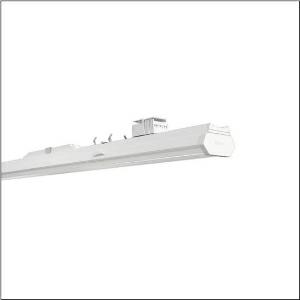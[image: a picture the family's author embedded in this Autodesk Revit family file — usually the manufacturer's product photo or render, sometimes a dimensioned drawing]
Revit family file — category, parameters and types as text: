
# Revit family: licross_21_protected_mo_52tp12dn4a5gd
name_source: partatom
category: Lighting Fixtures
units: mm (PartAtom-declared; Revit-internal decimal feet)

## family parameters
Cut with Voids When Loaded = No
Host = Face
Light Source = No
Part Type = Normal
Room Calculation Point = No
Round Connector Dimension = Use Diameter
Shared = No

## types (1)
- --- (1 x LED, 1610 lm, 10.2 W, 4000K)
    Apparent Load = 10 VA
    CIE Flux Codes = 73 92 98 99 100
    Color Rendering = 80
    Color Temperature = 4000K
    Default Elevation = 1800 mm
    Description = Licross 21 Protected MO, luminaire insert, of sheet steel, galvanised, coil coated, white, length: 1.500mm, width: 90mm, height: 103mm, LED rated luminous flux: 10.700lm, light colour: 840, SDCM (Standard Deviation of Colour Matching)MacAdam ≤ 3 SDCM (initial), control gear: DALI 2 (for two DALI lines), with plug, 6-pole, with phase selection, mains connection: 220..240V, AC/DC, 0/50..60Hz, rated input power: 62W, without changeover relay, for emergency light function, for central battery installations according to EN 60598-2-22, internal wiring halogen-free, primary light control with lens, of plastic, primary optical cover: cover, of PMMA, light emission: direct distribution, primary light characteristic: symmetric, protection rating (complete): IP64, insulation class (complete): insulation class I (protective earthing), certification: CE, ENEC, VDE, UKCA, protection symbol: D if used in an environment with conductive dust loads with corresponding accessories, impact resistance: IK06, permissible ambient temperature for indoor applications: -25..+35°C, standard: EN 60598-2-22, corresponds to IFS (International Featured Standards) requirements for safety and quality in the food industry, reducing of maximum allowable ambient temperature of 5°C with ceiling mounting, LABS conformity tested according to VDMA 24364:2018-05, The light source and the operating device comply with the requirements of the Ecodesign Regulation (EU) 2019/2020 and are replaceable in accordance with this regulation, packaging unit: 1 piece
    Height = 92 mm
    Lamp = 1 x LED
    Lamp Light Flux = 1610 lm
    Lamp Power = 10.2 W
    Lamp count = 1
    Length = 1500 mm
    Luminous efficacy = 158 lm/W
    Manufacturer = Siteco
    ModVariant = No
    Model = 52TP12DN4A5GD
    Mounting Place = Ceiling
    Mounting Type = Pendant
    Number of Poles = 1
    OnlyDefault = Yes
    Power Factor = 1
    Product Name = Licross 21 Protected MO
    Product group = luminaire insert | ceiling pendant
    ProductGroupID = 901
    Protection Class = Protection class I
    Protection Degree = IP 64
    RLX_Detail_Level = 1
    RLX_Emergency_Light_Flux = 0 lm
    RLX_Emergency_Type = 0
    RLX_Emergency_Type_DB = No
    RlxData = <blob elided: 25289 chars, md5=6200d928>
    Socket = socket
    Standby Power = 0 W
    System Light Flux = 1610 lm
    System Power = 10 W
    Type Comments = : DC mode (central or group accumulator) initial emergency light level
    Type Image = l_1256148.jpg
    URL = http://relux.com
    VarID = @adj_116425
    Voltage = 0 V
    Weight = 0.00 kg
    Width = 88 mm

## geometry (parser evidence)
native form markers: Blend x4, Sweep x10
no freeform markers — native parametric forms only
